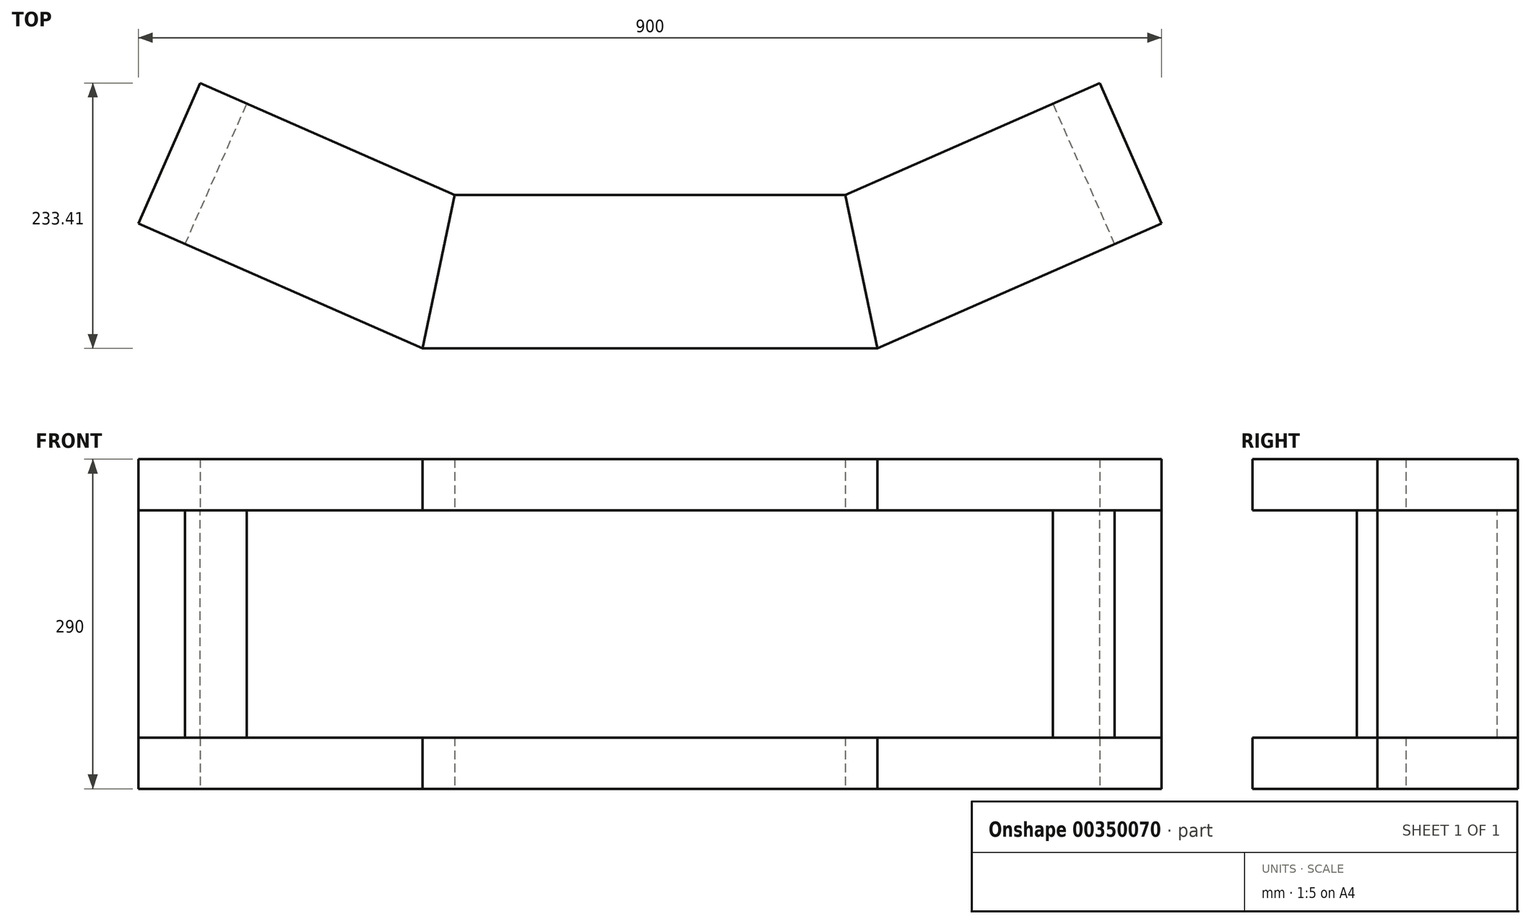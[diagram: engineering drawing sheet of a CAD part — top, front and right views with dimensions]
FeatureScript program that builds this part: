
annotation { "Feature Type Name" : "Feature", "Feature Type Description" : "" }
export const myFeature = defineFeature(function(context is Context, id is Id, definition is map)
    precondition{}
    {
        {
            var Q0;
            Q0=qCreatedBy(makeId("Top.planeOp"),FACE);
            var sketch = newSketch(context, id + "F0", { "sketchPlane" : qUnion([Q0])});
            skLineSegment(sketch, "E0.bottom", {"start": v(-200, 0) * mm, "end": v(0, 0) * mm});
            skLineSegment(sketch, "E0.top", {"start": v(-171.66, 135) * mm, "end": v(0, 135) * mm});
            skLineSegment(sketch, "E1", {"start": v(-200, 0) * mm, "end": v(-450, 109.8) * mm});
            skLineSegment(sketch, "E2", {"start": v(-450, 109.8) * mm, "end": v(-395.71, 233.4) * mm});
            skLineSegment(sketch, "E3", {"start": v(-395.71, 233.4) * mm, "end": v(-171.66, 135) * mm});
            skLineSegment(sketch, "E4", {"start": v(0, 0) * mm, "end": v(0, 223.61) * mm, "construction": true});
            skLineSegment(sketch, "E5", {"start": v(-200, 0) * mm, "end": v(-171.66, 135) * mm});
            skLineSegment(sketch, "E6.MirrorCS", {"start": v(200, 0) * mm, "end": v(0, 0) * mm});
            skLineSegment(sketch, "E7.MirrorCS", {"start": v(171.66, 135) * mm, "end": v(0, 135) * mm});
            skLineSegment(sketch, "E8.MirrorCS", {"start": v(450, 109.8) * mm, "end": v(395.71, 233.4) * mm});
            skLineSegment(sketch, "E9.MirrorCS", {"start": v(200, 0) * mm, "end": v(450, 109.8) * mm});
            skLineSegment(sketch, "E10.MirrorCS", {"start": v(395.71, 233.4) * mm, "end": v(171.66, 135) * mm});
            skLineSegment(sketch, "E11.MirrorCS", {"start": v(200, 0) * mm, "end": v(171.66, 135) * mm});
            skLineSegment(sketch, "E12", {"start": v(-325, 54.9) * mm, "end": v(-241.2, 245.7) * mm, "construction": true});
            skSolve(sketch);
        }
        {
            var Q0;
            Q0=makeQuery(id+"F0.imprint","IMPRINT",FACE,{"disambiguationData":[TD([[makeQuery(id+"F0.imprint","IMPRINT",EDGE,{"derivedFrom":sQuery(id+"F0.wireOp",EDGE,"E1")}),-1.0]])]});
            extrude(context, id + "F1", {"entities" : qUnion([Q0]), "depth" : 45 * mm});
        }
        {
            var Q0;
            Q0=makeQuery(id+"F0.imprint","IMPRINT",FACE,{"disambiguationData":[TD([[makeQuery(id+"F0.imprint","IMPRINT",EDGE,{"derivedFrom":sQuery(id+"F0.wireOp",EDGE,"E0.bottom")}),1.0]])]});
            extrude(context, id + "F2", {"entities" : qUnion([Q0]), "depth" : 45 * mm});
        }
        {
            var Q0;
            Q0=makeQuery(id+"F0.imprint","IMPRINT",FACE,{"disambiguationData":[TD([[makeQuery(id+"F0.imprint","IMPRINT",EDGE,{"derivedFrom":sQuery(id+"F0.wireOp",EDGE,"E8.MirrorCS")}),1.0]])]});
            extrude(context, id + "F3", {"entities" : qUnion([Q0]), "depth" : 45 * mm});
        }
        {
            var Q0;
            Q0=makeQuery(id+"F0.imprint","IMPRINT",FACE,{"disambiguationData":[TD([[makeQuery(id+"F0.imprint","IMPRINT",EDGE,{"derivedFrom":sQuery(id+"F0.wireOp",EDGE,"E8.MirrorCS")}),1.0]])]});
            var sketch = newSketch(context, id + "F4", { "sketchPlane" : qUnion([Q0])});
            skLineSegment(sketch, "E13", {"start": v(450, 109.8) * mm, "end": v(395.71, 233.4) * mm});
            skLineSegment(sketch, "E14", {"start": v(450, 109.8) * mm, "end": v(408.8, 91.7) * mm});
            skLineSegment(sketch, "E15", {"start": v(408.8, 91.7) * mm, "end": v(354.51, 215.31) * mm});
            skLineSegment(sketch, "E16", {"start": v(354.51, 215.31) * mm, "end": v(395.71, 233.4) * mm});
            skSolve(sketch);
        }
        {
            var Q0;
            Q0 = qSketchRegion(id + "F4", true);
            extrude(context, id + "F5", {"entities" : qUnion([Q0]), "oppositeDirection" : true, "depth" : 200 * mm});
        }
        {
            var Q0;
            Q0=makeQuery(id+"F5.opExtrude","SWEPT_BODY",BODY,{"disambiguationData":[OSD([sQuery(id+"F4.wireOp",EDGE,"E13"),sQuery(id+"F4.wireOp",EDGE,"E14"),sQuery(id+"F4.wireOp",EDGE,"E15"),sQuery(id+"F4.wireOp",EDGE,"E16")])]});
            var Q1;
            Q1=qCreatedBy(makeId("Right.planeOp"),FACE);
            mirror(context, id + "F6", {"entities" : qUnion([Q0]), "mirrorPlane" : qUnion([Q1])});
        }
        {
            var Q0;
            Q0=makeQuery(id+"F1.opExtrude","SWEPT_BODY",BODY,{"disambiguationData":[OSD([sQuery(id+"F0.wireOp",EDGE,"E1"),sQuery(id+"F0.wireOp",EDGE,"E2"),sQuery(id+"F0.wireOp",EDGE,"E3"),sQuery(id+"F0.wireOp",EDGE,"E5")])]});
            var Q1;
            Q1=makeQuery(id+"F2.opExtrude","SWEPT_BODY",BODY,{"disambiguationData":[OSD([sQuery(id+"F0.wireOp",EDGE,"E0.bottom"),sQuery(id+"F0.wireOp",EDGE,"E0.top"),sQuery(id+"F0.wireOp",EDGE,"E5"),sQuery(id+"F0.wireOp",EDGE,"E6.MirrorCS"),sQuery(id+"F0.wireOp",EDGE,"E7.MirrorCS"),sQuery(id+"F0.wireOp",EDGE,"E11.MirrorCS")])]});
            var Q2;
            Q2=makeQuery(id+"F3.opExtrude","SWEPT_BODY",BODY,{"disambiguationData":[OSD([sQuery(id+"F0.wireOp",EDGE,"E8.MirrorCS"),sQuery(id+"F0.wireOp",EDGE,"E9.MirrorCS"),sQuery(id+"F0.wireOp",EDGE,"E10.MirrorCS"),sQuery(id+"F0.wireOp",EDGE,"E11.MirrorCS")])]});
            var Q3;
            Q3=qCreatedBy(makeId("Top.planeOp"),FACE);
            transform(context, id + "F7", {"entities" : qUnion([Q0, Q1, Q2]), "transformType" : TransformType.TRANSLATION_DISTANCE, "transformDirection" : qUnion([Q3]), "distance" : 245 * mm, "oppositeDirection" : true, "makeCopy" : true});
        }
    });
